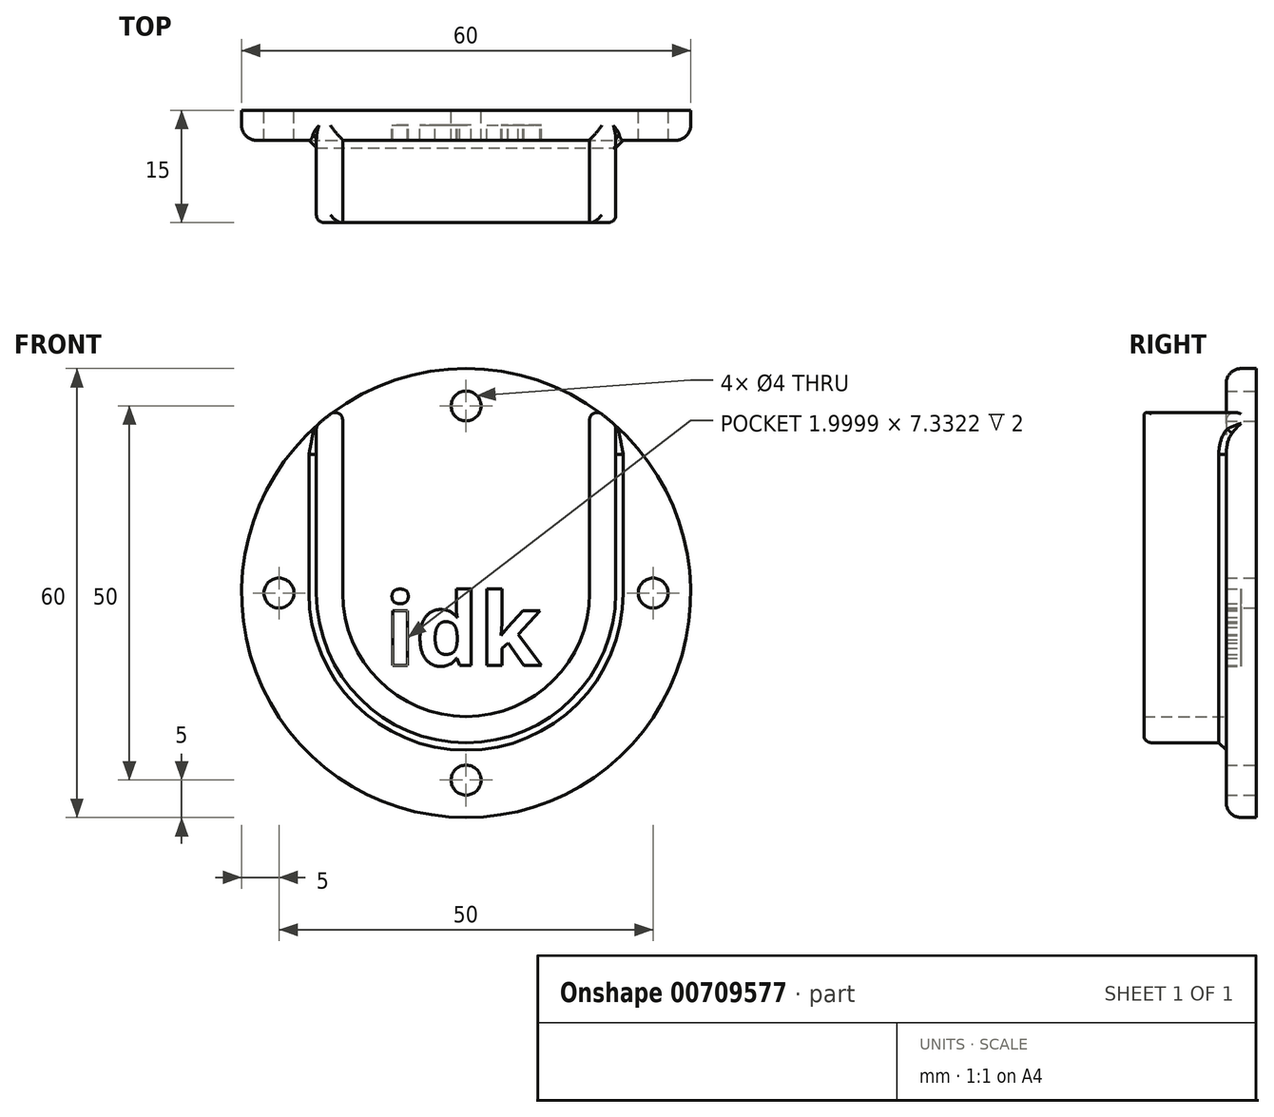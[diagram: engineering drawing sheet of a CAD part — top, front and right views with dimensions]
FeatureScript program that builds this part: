
annotation { "Feature Type Name" : "Feature", "Feature Type Description" : "" }
export const myFeature = defineFeature(function(context is Context, id is Id, definition is map)
    precondition{}
    {
        {
            var Q0;
            Q0=qCreatedBy(makeId("Front.planeOp"),FACE);
            var sketch = newSketch(context, id + "F0", { "sketchPlane" : qUnion([Q0])});
            skCircle(sketch, "E0", {"center": v(0, 0) * mm, "radius": 16.5 * mm});
            skCircle(sketch, "E1", {"center": v(0, 0) * mm, "radius": 20 * mm});
            skCircle(sketch, "E2", {"center": v(0, 0) * mm, "radius": 30 * mm});
            skLineSegment(sketch, "E3", {"start": v(-20, 0) * mm, "end": v(-20, 22.36) * mm});
            skLineSegment(sketch, "E4", {"start": v(-16.5, 0) * mm, "end": v(-16.5, 25.05) * mm});
            skLineSegment(sketch, "E5", {"start": v(20, 0) * mm, "end": v(20, 22.36) * mm});
            skLineSegment(sketch, "E6", {"start": v(16.5, 0) * mm, "end": v(16.5, 25.05) * mm});
            skCircle(sketch, "E7", {"center": v(-25, 0) * mm, "radius": 2 * mm});
            skCircle(sketch, "E8", {"center": v(0, -25) * mm, "radius": 2 * mm});
            skCircle(sketch, "E9", {"center": v(25, 0) * mm, "radius": 2 * mm});
            skCircle(sketch, "E10", {"center": v(0, 25) * mm, "radius": 2 * mm});
            skSolve(sketch);
        }
        {
            var Q0;
            {var subQ1=sQuery(id+"F0.wireOp",EDGE,"E3");Q0=makeQuery(id+"F0.imprint","IMPRINT",FACE,{"disambiguationData":[TD([[makeQuery(id+"F0.imprint","IMPRINT",EDGE,{"derivedFrom":subQ1}),1.0]])]});}
            var Q1;
            Q1=makeQuery(id+"F0.imprint","IMPRINT",FACE,{"disambiguationData":[TD([[makeQuery(id+"F0.imprint","IMPRINT",EDGE,{"derivedFrom":sQuery(id+"F0.wireOp",EDGE,"E10")}),-1.0]])]});
            var Q2;
            {var subQ0=sQuery(id+"F0.wireOp",EDGE,"E4");var subQ1=sQuery(id+"F0.wireOp",EDGE,"E0");var subQ2=makeQuery(id+"F0.imprint","INTERSECT",VERTEX,{"derivedFrom":[subQ1,subQ0]});Q2=makeQuery(id+"F0.imprint","IMPRINT",FACE,{"disambiguationData":[TD([[makeQuery(id+"F0.imprint","IMPRINT",EDGE,{"disambiguationData":[TD([[subQ2,1.0]])],"derivedFrom":subQ1}),-1.0]])]});}
            var Q3;
            {var subQ0=sQuery(id+"F0.wireOp",EDGE,"E0");var subQ1=makeQuery(id+"F0.imprint","INTERSECT",VERTEX,{"derivedFrom":[subQ0,sQuery(id+"F0.wireOp",EDGE,"E4")]});Q3=makeQuery(id+"F0.imprint","IMPRINT",FACE,{"disambiguationData":[TD([[makeQuery(id+"F0.imprint","IMPRINT",EDGE,{"disambiguationData":[TD([[subQ1,1.0]])],"derivedFrom":subQ0}),1.0]])]});}
            var Q4;
            {var subQ3=sQuery(id+"F0.wireOp",EDGE,"E4");var subQ7=sQuery(id+"F0.wireOp",EDGE,"E0");var subQ8=makeQuery(id+"F0.imprint","INTERSECT",VERTEX,{"derivedFrom":[subQ7,subQ3]});Q4=makeQuery(id+"F0.imprint","IMPRINT",FACE,{"disambiguationData":[TD([[makeQuery(id+"F0.imprint","IMPRINT",EDGE,{"disambiguationData":[TD([[subQ8,-1.0]])],"derivedFrom":subQ7}),-1.0]])]});}
            var Q5;
            {var subQ0=sQuery(id+"F0.wireOp",EDGE,"E5");Q5=makeQuery(id+"F0.imprint","IMPRINT",FACE,{"disambiguationData":[TD([[makeQuery(id+"F0.imprint","IMPRINT",EDGE,{"derivedFrom":subQ0}),1.0]])]});}
            var Q6;
            {var subQ0=sQuery(id+"F0.wireOp",EDGE,"E3");Q6=makeQuery(id+"F0.imprint","IMPRINT",FACE,{"disambiguationData":[TD([[makeQuery(id+"F0.imprint","IMPRINT",EDGE,{"derivedFrom":subQ0}),-1.0]])]});}
            extrude(context, id + "F1", {"entities" : qUnion([Q0, Q1, Q2, Q3, Q4, Q5, Q6]), "depth" : 4 * mm, "offsetDistance" : 25.4 * mm});
        }
        {
            var Q0;
            {var subQ0=sQuery(id+"F0.wireOp",EDGE,"E2");Q0=makeQuery(id+"F1.opExtrude","CAP_EDGE",EDGE,{"disambiguationData":[OSD([subQ0]),TDD([makeQuery(id+"F0.imprint","IMPRINT",EDGE,{"disambiguationData":[TD([[makeQuery(id+"F0.imprint","INTERSECT",VERTEX,{"derivedFrom":[subQ0,sQuery(id+"F0.wireOp",EDGE,"E3")]}),-1.0]])],"derivedFrom":subQ0})])],"isStart":false});}
            var Q1;
            {var subQ0=sQuery(id+"F0.wireOp",EDGE,"E2");Q1=makeQuery(id+"F1.opExtrude","CAP_EDGE",EDGE,{"disambiguationData":[OSD([subQ0]),TDD([makeQuery(id+"F0.imprint","IMPRINT",EDGE,{"disambiguationData":[TD([[makeQuery(id+"F0.imprint","INTERSECT",VERTEX,{"derivedFrom":[subQ0,sQuery(id+"F0.wireOp",EDGE,"E4")]}),1.0]])],"derivedFrom":subQ0})])],"isStart":false});}
            fillet(context, id + "F2", {"entities" : qUnion([Q0, Q1]), "radius" : 2 * mm, "tangentPropagation" : true, "allowEdgeOverflow" : false});
        }
        {
            var Q0;
            {var subQ0=sQuery(id+"F0.wireOp",EDGE,"E3");Q0=makeQuery(id+"F0.imprint","IMPRINT",FACE,{"disambiguationData":[TD([[makeQuery(id+"F0.imprint","IMPRINT",EDGE,{"derivedFrom":subQ0}),-1.0]])]});}
            var Q1;
            {var subQ3=sQuery(id+"F0.wireOp",EDGE,"E4");var subQ7=sQuery(id+"F0.wireOp",EDGE,"E0");var subQ8=makeQuery(id+"F0.imprint","INTERSECT",VERTEX,{"derivedFrom":[subQ7,subQ3]});Q1=makeQuery(id+"F0.imprint","IMPRINT",FACE,{"disambiguationData":[TD([[makeQuery(id+"F0.imprint","IMPRINT",EDGE,{"disambiguationData":[TD([[subQ8,-1.0]])],"derivedFrom":subQ7}),-1.0]])]});}
            var Q2;
            {var subQ0=sQuery(id+"F0.wireOp",EDGE,"E5");Q2=makeQuery(id+"F0.imprint","IMPRINT",FACE,{"disambiguationData":[TD([[makeQuery(id+"F0.imprint","IMPRINT",EDGE,{"derivedFrom":subQ0}),1.0]])]});}
            extrude(context, id + "F3", {"entities" : qUnion([Q0, Q1, Q2]), "operationType" : NewBodyOperationType.ADD, "depth" : 15 * mm, "offsetDistance" : 25.4 * mm});
        }
        {
            var Q0;
            {var subQ0=sQuery(id+"F0.wireOp",EDGE,"E2");Q0=makeQuery(id+"F3.opExtrude","CAP_EDGE",EDGE,{"disambiguationData":[OSD([subQ0]),TDD([makeQuery(id+"F0.imprint","IMPRINT",EDGE,{"disambiguationData":[TD([[makeQuery(id+"F0.imprint","INTERSECT",VERTEX,{"derivedFrom":[subQ0,sQuery(id+"F0.wireOp",EDGE,"E3")]}),1.0]])],"derivedFrom":subQ0})])],"isStart":false});}
            var Q1;
            Q1=makeQuery(id+"F3.opExtrude","CAP_EDGE",EDGE,{"disambiguationData":[OSD([sQuery(id+"F0.wireOp",EDGE,"E3")])],"isStart":false});
            var Q2;
            {var subQ0=sQuery(id+"F0.wireOp",EDGE,"E2");Q2=makeQuery(id+"F3.opExtrude","CAP_EDGE",EDGE,{"disambiguationData":[OSD([subQ0]),TDD([makeQuery(id+"F0.imprint","IMPRINT",EDGE,{"disambiguationData":[TD([[makeQuery(id+"F0.imprint","INTERSECT",VERTEX,{"derivedFrom":[subQ0,sQuery(id+"F0.wireOp",EDGE,"E5")]}),-1.0]])],"derivedFrom":subQ0})])],"isStart":false});}
            var Q3;
            Q3=makeQuery(id+"F3.opExtrude","SWEPT_EDGE",EDGE,{"disambiguationData":[OSD([sQuery(id+"F0.wireOp",EDGE,"E2"),sQuery(id+"F0.wireOp",EDGE,"E3")])]});
            var Q4;
            Q4=makeQuery(id+"F3.opExtrude","SWEPT_EDGE",EDGE,{"disambiguationData":[OSD([sQuery(id+"F0.wireOp",EDGE,"E2"),sQuery(id+"F0.wireOp",EDGE,"E4")])]});
            var Q5;
            Q5=makeQuery(id+"F3.opExtrude","SWEPT_EDGE",EDGE,{"disambiguationData":[OSD([sQuery(id+"F0.wireOp",EDGE,"E2"),sQuery(id+"F0.wireOp",EDGE,"E6")])]});
            var Q6;
            Q6=makeQuery(id+"F3.opExtrude","SWEPT_EDGE",EDGE,{"disambiguationData":[OSD([sQuery(id+"F0.wireOp",EDGE,"E2"),sQuery(id+"F0.wireOp",EDGE,"E5")])]});
            fillet(context, id + "F4", {"entities" : qUnion([Q0, Q1, Q2, Q3, Q4, Q5, Q6]), "radius" : 1 * mm, "tangentPropagation" : true, "allowEdgeOverflow" : false});
        }
        {
            var Q0;
            Q0=makeQuery(id+"F3.boolean.opBoolean","INTERSECT",EDGE,{"derivedFrom":[makeQuery(id+"F1.opExtrude","CAP_FACE",FACE,{"disambiguationData":[OSD([sQuery(id+"F0.wireOp",EDGE,"E2"),sQuery(id+"F0.wireOp",EDGE,"E7"),sQuery(id+"F0.wireOp",EDGE,"E8"),sQuery(id+"F0.wireOp",EDGE,"E9"),sQuery(id+"F0.wireOp",EDGE,"E10")])],"isStart":false}),makeQuery(id+"F3.opExtrude","SWEPT_FACE",FACE,{"disambiguationData":[OSD([sQuery(id+"F0.wireOp",EDGE,"E3")])]})]});
            var Q1;
            Q1=makeQuery(id+"F3.boolean.opBoolean","INTERSECT",EDGE,{"derivedFrom":[makeQuery(id+"F1.opExtrude","CAP_FACE",FACE,{"disambiguationData":[OSD([sQuery(id+"F0.wireOp",EDGE,"E2"),sQuery(id+"F0.wireOp",EDGE,"E7"),sQuery(id+"F0.wireOp",EDGE,"E8"),sQuery(id+"F0.wireOp",EDGE,"E9"),sQuery(id+"F0.wireOp",EDGE,"E10")])],"isStart":false}),makeQuery(id+"F3.opExtrude","SWEPT_FACE",FACE,{"disambiguationData":[OSD([sQuery(id+"F0.wireOp",EDGE,"E1")])]})]});
            var Q2;
            Q2=makeQuery(id+"F3.boolean.opBoolean","INTERSECT",EDGE,{"derivedFrom":[makeQuery(id+"F1.opExtrude","CAP_FACE",FACE,{"disambiguationData":[OSD([sQuery(id+"F0.wireOp",EDGE,"E2"),sQuery(id+"F0.wireOp",EDGE,"E7"),sQuery(id+"F0.wireOp",EDGE,"E8"),sQuery(id+"F0.wireOp",EDGE,"E9"),sQuery(id+"F0.wireOp",EDGE,"E10")])],"isStart":false}),makeQuery(id+"F3.opExtrude","SWEPT_FACE",FACE,{"disambiguationData":[OSD([sQuery(id+"F0.wireOp",EDGE,"E5")])]})]});
            chamfer(context, id + "F5", {"entities" : qUnion([Q0, Q1, Q2]), "width" : 1 * mm, "tangentPropagation" : true});
        }
        {
            var Q0;
            Q0=qCreatedBy(makeId("Front.planeOp"),FACE);
            cPlane(context, id + "F6", {"entities" : qUnion([Q0]), "cplaneType" : CPlaneType.OFFSET, "offset" : 2 * mm, "width" : 150 * mm, "height" : 150 * mm});
        }
        {
            var Q0;
            Q0=qCreatedBy(id+"F6.planeOp",FACE);
            var sketch = newSketch(context, id + "F7", { "sketchPlane" : qUnion([Q0])});
            skText(sketch, "E11", { "text": "idk", "fontName": "OpenSans-Bold.ttf"});
            const initialGuessF7  = {"E11": [-0.01087, -0.00967, 1, 0, 0.00967]};
            skSetInitialGuess(sketch, initialGuessF7);
            skSolve(sketch);
        }
        {
            var Q0;
            Q0 = qSketchRegion(id + "F7", true);
            extrude(context, id + "F8", {"entities" : qUnion([Q0]), "operationType" : NewBodyOperationType.REMOVE, "oppositeDirection" : true, "depth" : -2 * mm, "offsetDistance" : 25 * mm});
        }
    });
